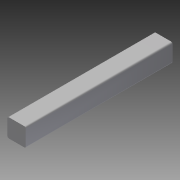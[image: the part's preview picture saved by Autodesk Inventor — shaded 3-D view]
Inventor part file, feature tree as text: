
AUTODESK INVENTOR PART (.ipt)
format: ipt  version: 2013 (Build 170138000, 138)  size: 76,800 bytes
history: native  units: in
note: dims shown in document units (in); Inventor stores cm internally (conversion verified against a paired STEP export)
features: extrude x1, fillet x1, sketch x1
ambient origin geometry x8: Origin, YZ Plane, XZ Plane, XY Plane, X Axis, Y Axis, Z Axis, Center Point
bodies: Solid1 (feature_tree)
feature tree (3):
  extrude  "Extrusion1"  Depth=1.0in TaperAngle=0.0deg
  fillet  "Fillet1"  Radius=0.01in
  sketch  "Sketch1"  dims[d0=0.125in d2=1.0in d3=0.0in d4=0.01in]
